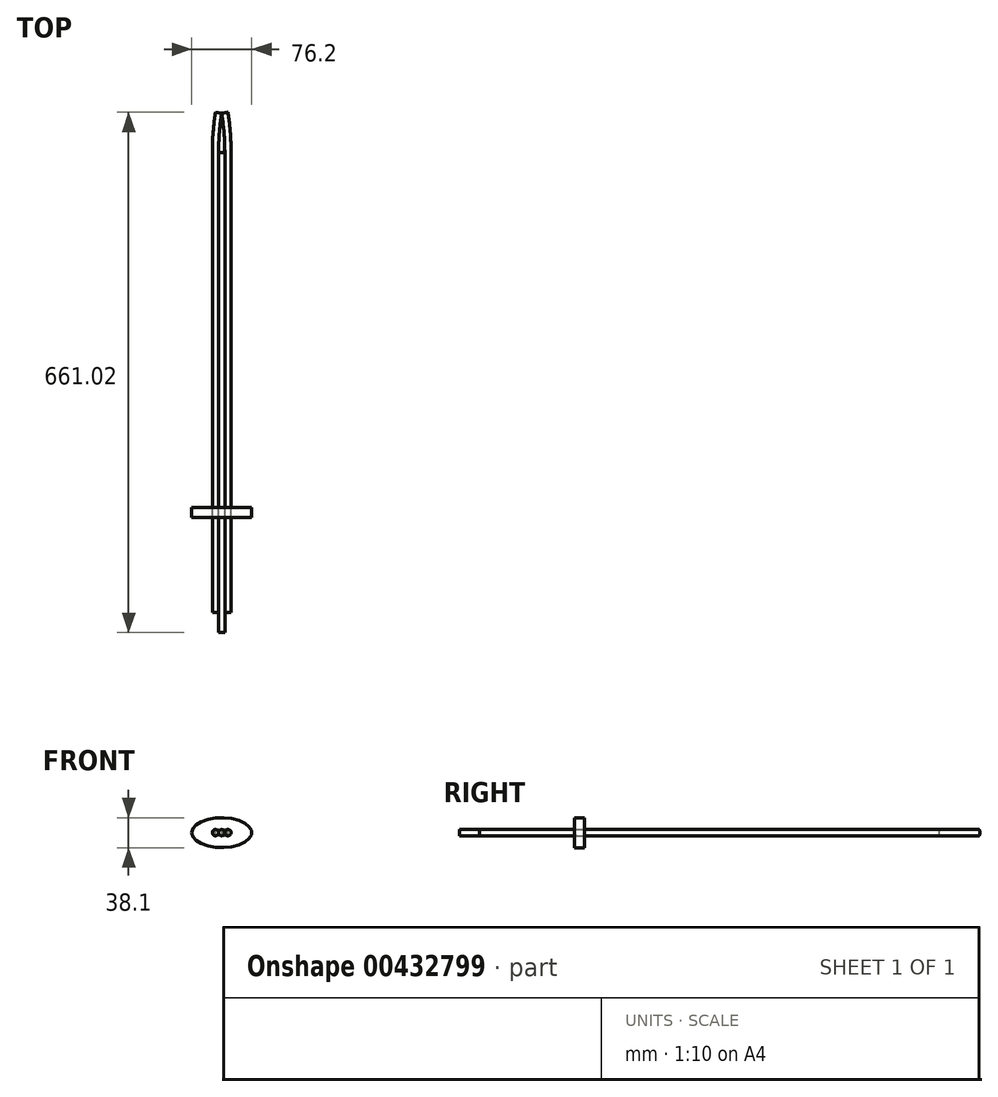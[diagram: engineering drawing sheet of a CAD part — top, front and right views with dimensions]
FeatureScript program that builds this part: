
annotation { "Feature Type Name" : "Feature", "Feature Type Description" : "" }
export const myFeature = defineFeature(function(context is Context, id is Id, definition is map)
    precondition{}
    {
        {
            var Q0;
            Q0=qCreatedBy(makeId("Top.planeOp"),FACE);
            var sketch = newSketch(context, id + "F0", { "sketchPlane" : qUnion([Q0])});
            skLineSegment(sketch, "E0.bottom", {"start": v(0, -25.4) * mm, "end": v(-3.97, -25.4) * mm});
            skLineSegment(sketch, "E0.top", {"start": v(0, 584.2) * mm, "end": v(-3.97, 584.2) * mm});
            skLineSegment(sketch, "E0.left", {"start": v(0, -25.4) * mm, "end": v(0, 584.2) * mm});
            skLineSegment(sketch, "E0.right", {"start": v(-3.97, -25.4) * mm, "end": v(-3.97, 584.2) * mm});
            skSolve(sketch);
        }
        {
            var Q0;
            Q0=makeQuery(id+"F0.imprint","IMPRINT",FACE,{"disambiguationData":[TD([[makeQuery(id+"F0.imprint","IMPRINT",EDGE,{"derivedFrom":sQuery(id+"F0.wireOp",EDGE,"E0.bottom")}),-1.0]])]});
            var Q1;
            Q1=sQuery(id+"F0.wireOp",EDGE,"E0.left");
            revolve(context, id + "F1", {"entities" : qUnion([Q0]), "axis" : qUnion([Q1]), "revolveType" : RevolveType.FULL});
        }
        {
            var Q0;
            Q0=qCreatedBy(makeId("Front.planeOp"),FACE);
            var sketch = newSketch(context, id + "F2", { "sketchPlane" : qUnion([Q0])});
            skCircle(sketch, "E1", {"center": v(7.94, 0) * mm, "radius": 3.97 * mm});
            skPoint(sketch, "E2", {"position": v(3.97, 0) * mm});
            skSolve(sketch);
        }
        {
            var Q0;
            Q0=qCreatedBy(makeId("Top.planeOp"),FACE);
            var sketch = newSketch(context, id + "F3", { "sketchPlane" : qUnion([Q0])});
            skLineSegment(sketch, "E3", {"start": v(7.94, 0) * mm, "end": v(7.94, 584.2) * mm});
            skArc(sketch, "E4", {"start": v(7.94, 584.2) * mm, "mid": v(6.94, 609.68) * mm, "end": v(3.97, 635) * mm});
            skLineSegment(sketch, "E5.0", {"start": v(3.97, 584.2) * mm, "end": v(-3.97, 584.2) * mm, "construction": true});
            skSolve(sketch);
        }
        {
            var Q0;
            Q0=makeQuery(id+"F2.imprint","IMPRINT",FACE,{"disambiguationData":[TD([[makeQuery(id+"F2.imprint","IMPRINT",EDGE,{"derivedFrom":sQuery(id+"F2.wireOp",EDGE,"E1")}),1.0]])]});
            var Q1;
            Q1 = qConstructionFilter(qBodyType(qCreatedBy(id + "F3" ,EDGE), BodyType.WIRE), ConstructionObject.NO);
            sweep(context, id + "F4", {"operationType" : NewBodyOperationType.ADD, "profiles" : qUnion([Q0]), "path" : qUnion([Q1])});
        }
        {
            var Q0;
            Q0=makeQuery(id+"F4.opSweep","SWEPT_BODY",BODY,{"disambiguationData":[OSD([sQuery(id+"F2.wireOp",EDGE,"E1"),sQuery(id+"F3.wireOp",EDGE,"E4")])]});
            var Q1;
            Q1=qCreatedBy(makeId("Right.planeOp"),FACE);
            mirror(context, id + "F5", {"entities" : qUnion([Q0]), "mirrorPlane" : qUnion([Q1])});
        }
        {
            var Q0;
            Q0=qCreatedBy(makeId("Front.planeOp"),FACE);
            cPlane(context, id + "F6", {"entities" : qUnion([Q0]), "cplaneType" : CPlaneType.OFFSET, "offset" : 127 * mm, "oppositeDirection" : true, "width" : 152.4 * mm, "height" : 152.4 * mm});
        }
        {
            var Q0;
            Q0=qCreatedBy(id+"F6.planeOp",FACE);
            var sketch = newSketch(context, id + "F7", { "sketchPlane" : qUnion([Q0])});
            skEllipse(sketch, "E6", {"center": v(0, 0) * mm, "majorRadius": 38.1 * mm, "minorRadius": 19.05 * mm, "majorAxis": v(-1, 0)});
            skSolve(sketch);
        }
        {
            var Q0;
            Q0 = qSketchRegion(id + "F7", true);
            extrude(context, id + "F8", {"entities" : qUnion([Q0]), "endBound" : BoundingType.SYMMETRIC, "depth" : 12.7 * mm});
        }
    });
